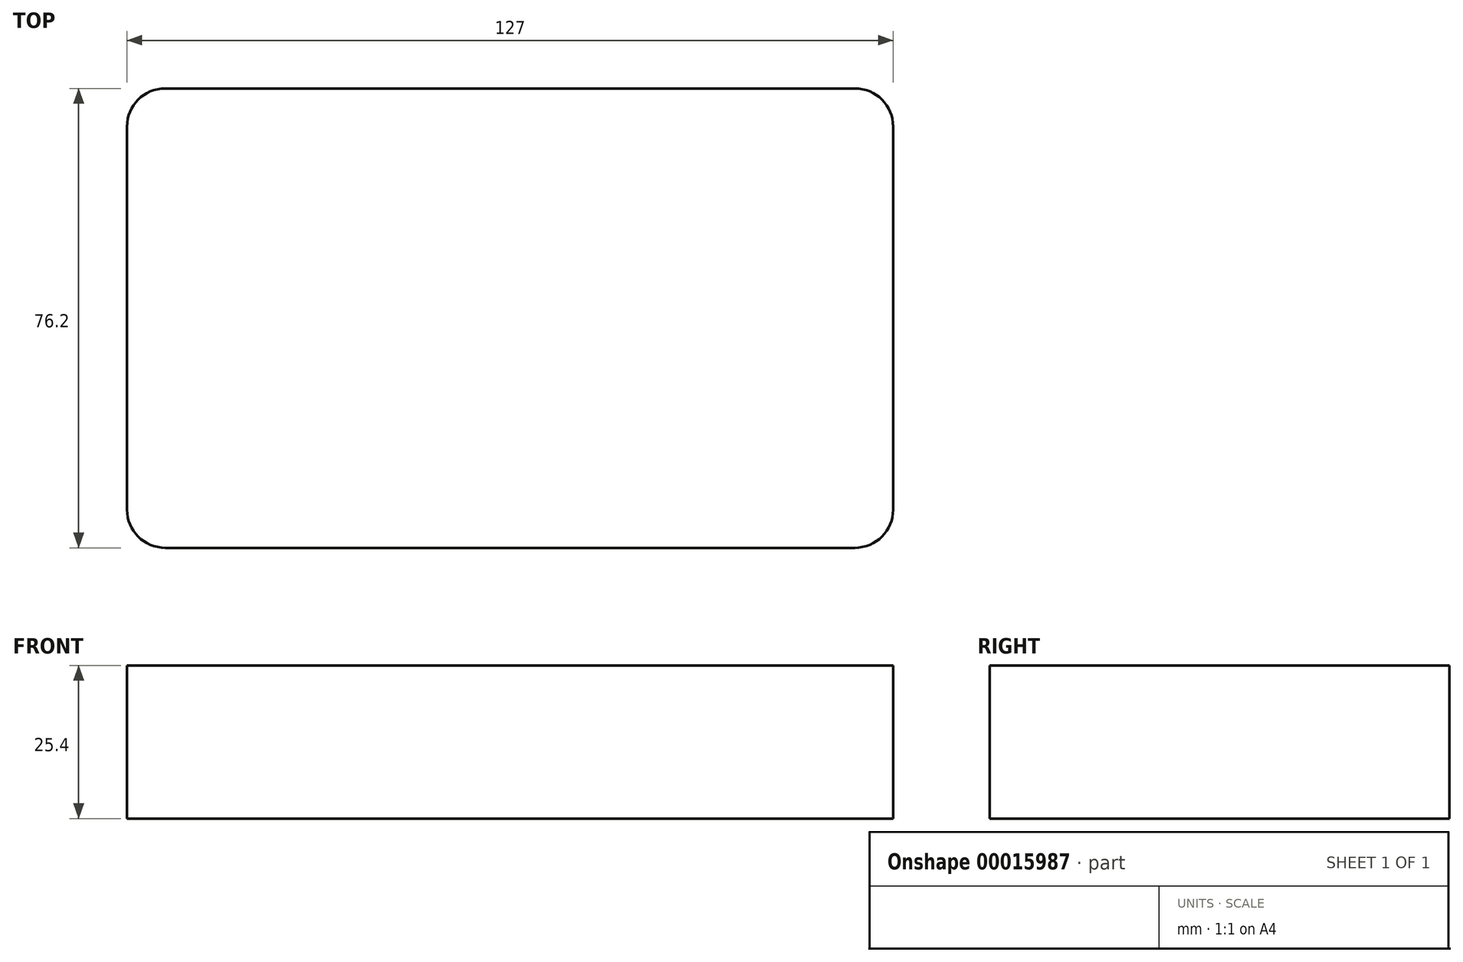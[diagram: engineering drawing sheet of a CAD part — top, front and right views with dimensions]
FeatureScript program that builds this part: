
annotation { "Feature Type Name" : "Feature", "Feature Type Description" : "" }
export const myFeature = defineFeature(function(context is Context, id is Id, definition is map)
    precondition{}
    {
        {
            var Q0;
            Q0=qCreatedBy(makeId("Top.planeOp"),FACE);
            var sketch = newSketch(context, id + "F0", { "sketchPlane" : qUnion([Q0])});
            skLineSegment(sketch, "E0.rect.bottom", {"start": v(-57.15, -38.1) * mm, "end": v(57.15, -38.1) * mm});
            skLineSegment(sketch, "E0.rect.top", {"start": v(-57.15, 38.1) * mm, "end": v(57.15, 38.1) * mm});
            skLineSegment(sketch, "E0.rect.left", {"start": v(-63.5, -31.75) * mm, "end": v(-63.5, 31.75) * mm});
            skLineSegment(sketch, "E0.rect.right", {"start": v(63.5, -31.75) * mm, "end": v(63.5, 31.75) * mm});
            skPoint(sketch, "E0.rect.middle", {"position": v(0, 0) * mm});
            skPoint(sketch, "E1.visualSharp", {"position": v(-63.5, 38.1) * mm});
            skArc(sketch, "E1.filletArc", {"start": v(-57.15, 38.1) * mm, "mid": v(-61.64, 36.24) * mm, "end": v(-63.5, 31.75) * mm});
            skPoint(sketch, "E2.visualSharp", {"position": v(-63.5, -38.1) * mm});
            skArc(sketch, "E2.filletArc", {"start": v(-63.5, -31.75) * mm, "mid": v(-61.64, -36.24) * mm, "end": v(-57.15, -38.1) * mm});
            skPoint(sketch, "E3.visualSharp", {"position": v(63.5, -38.1) * mm});
            skArc(sketch, "E3.filletArc", {"start": v(57.15, -38.1) * mm, "mid": v(61.64, -36.24) * mm, "end": v(63.5, -31.75) * mm});
            skPoint(sketch, "E4.visualSharp", {"position": v(63.5, 38.1) * mm});
            skArc(sketch, "E4.filletArc", {"start": v(63.5, 31.75) * mm, "mid": v(61.64, 36.24) * mm, "end": v(57.15, 38.1) * mm});
            skSolve(sketch);
        }
        {
            var Q0;
            Q0=makeQuery(id+"F0.imprint","IMPRINT",FACE,{"disambiguationData":[TD([[makeQuery(id+"F0.imprint","IMPRINT",EDGE,{"derivedFrom":sQuery(id+"F0.wireOp",EDGE,"E0.rect.bottom")}),1.0]])]});
            extrude(context, id + "F1", {"entities" : qUnion([Q0]), "depth" : 25.4 * mm});
        }
    });
